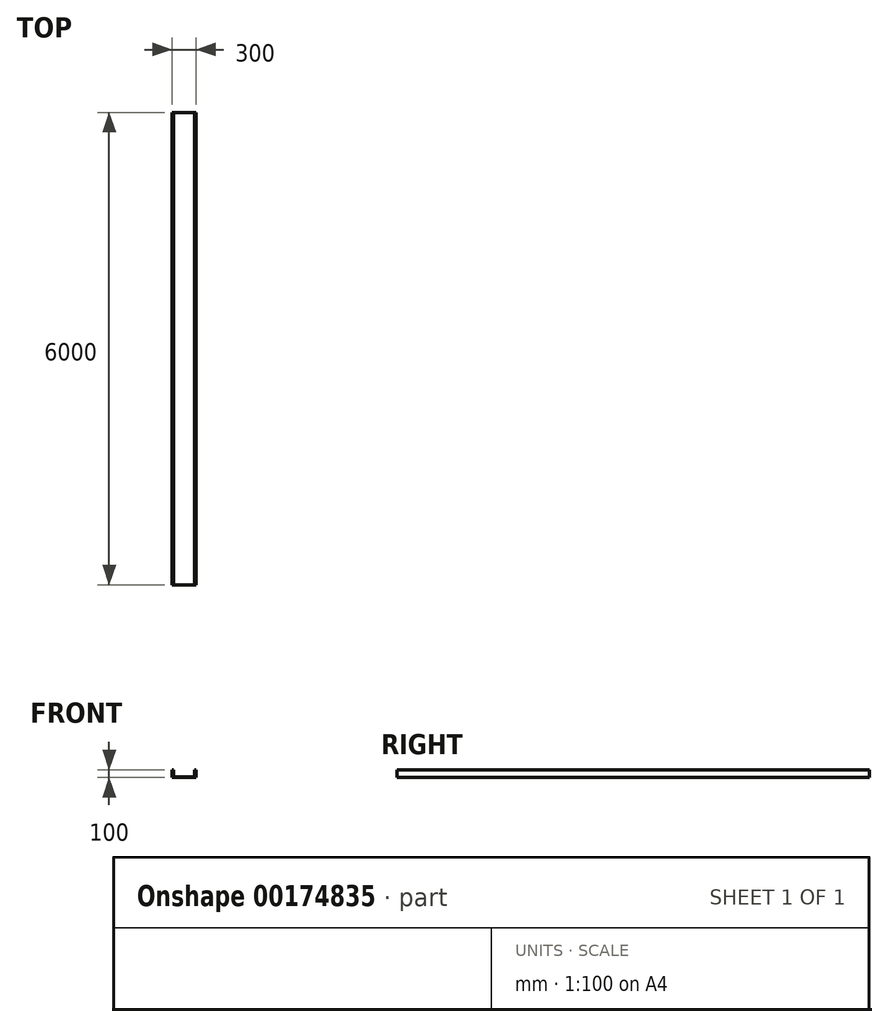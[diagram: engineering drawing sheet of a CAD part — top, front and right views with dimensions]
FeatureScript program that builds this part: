
annotation { "Feature Type Name" : "Feature", "Feature Type Description" : "" }
export const myFeature = defineFeature(function(context is Context, id is Id, definition is map)
    precondition{}
    {
        {
            var Q0;
            Q0=qCreatedBy(makeId("Front.planeOp"),FACE);
            var sketch = newSketch(context, id + "F0", { "sketchPlane" : qUnion([Q0])});
            skLineSegment(sketch, "E0", {"start": v(0, 0) * mm, "end": v(300, 0) * mm});
            skLineSegment(sketch, "E1", {"start": v(300, 0) * mm, "end": v(300, 100) * mm});
            skLineSegment(sketch, "E2", {"start": v(300, 100) * mm, "end": v(285, 100) * mm});
            skLineSegment(sketch, "E3", {"start": v(285, 100) * mm, "end": v(285, 9.5) * mm});
            skLineSegment(sketch, "E4", {"start": v(285, 9.5) * mm, "end": v(15, 9.5) * mm});
            skLineSegment(sketch, "E5", {"start": v(15, 9.5) * mm, "end": v(15, 100) * mm});
            skLineSegment(sketch, "E6", {"start": v(15, 100) * mm, "end": v(0, 100) * mm});
            skLineSegment(sketch, "E7", {"start": v(0, 100) * mm, "end": v(0, 0) * mm});
            skSolve(sketch);
        }
        {
            var Q0;
            Q0 = qSketchRegion(id + "F0", true);
            extrude(context, id + "F1", {"entities" : qUnion([Q0]), "depth" : 6000 * mm});
        }
    });
